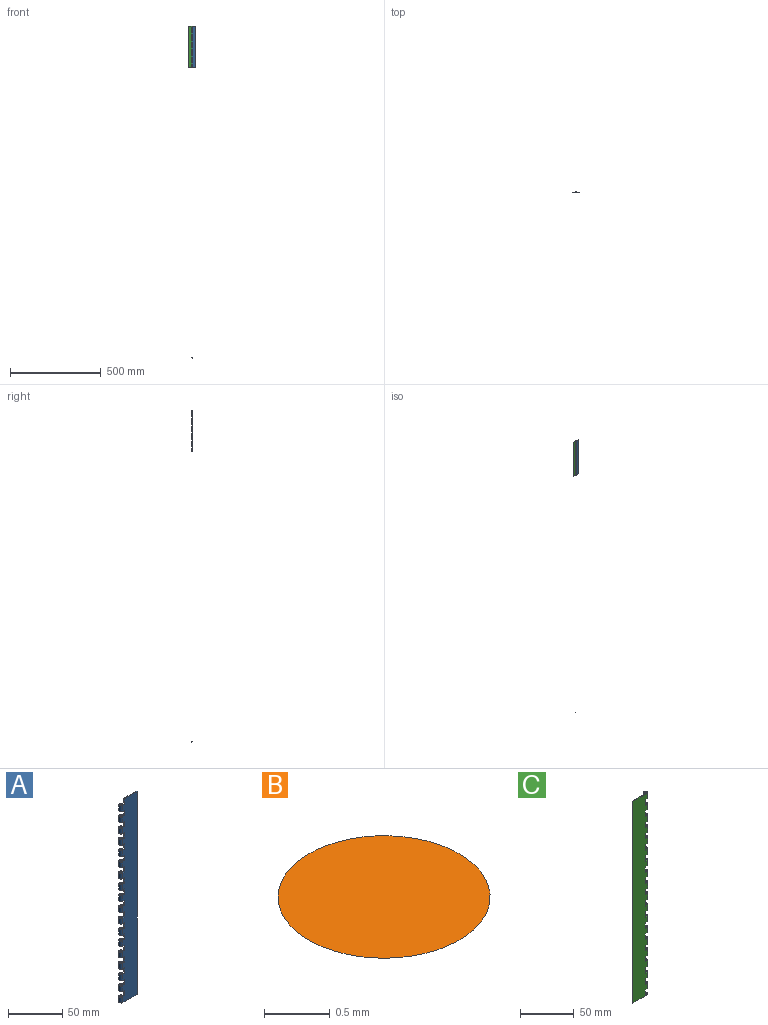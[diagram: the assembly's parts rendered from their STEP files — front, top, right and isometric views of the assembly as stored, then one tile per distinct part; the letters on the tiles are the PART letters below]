
ASSEMBLY  parts=3 mates=2
PART A: 96 faces, bbox 21x3.9x228.8 mm
  f0: plane 228.8x17.4mm, normal (0,1,0), area 3893.9mm2, adj f2,f3,f5,f7,f9,f11,f13,f15
  f1: plane 228.8x19.05mm, normal (0,-1,0), area 4081.5mm2, adj f2,f3,f5,f7,f9,f11,f13,f15
  f2: plane 228.8x0.89mm, normal (1,0,0), area 203.4mm2, adj f0,f1,f39,f95
  f3: cylinder r=1.97mm len=6.33mm, axis (0,0,-1), area 66mm2, adj f0,f1,f91,f94
  f4: cylinder r=1.08mm len=6.33mm, axis (0,0,-1), area 42.9mm2, adj f91,f94
  f5: cylinder r=1.97mm len=6.33mm, axis (0,0,-1), area 66mm2, adj f0,f1,f88,f92
  f6: cylinder r=1.08mm len=6.33mm, axis (0,0,-1), area 42.9mm2, adj f88,f92
  f7: cylinder r=1.97mm len=6.33mm, axis (0,0,-1), area 66mm2, adj f0,f1,f85,f89
  f8: cylinder r=1.08mm len=6.33mm, axis (0,0,-1), area 42.9mm2, adj f85,f89
  f9: cylinder r=1.97mm len=6.33mm, axis (0,0,-1), area 66mm2, adj f0,f1,f82,f86
  f10: cylinder r=1.08mm len=6.33mm, axis (0,0,-1), area 42.9mm2, adj f82,f86
  f11: cylinder r=1.97mm len=6.33mm, axis (0,0,-1), area 66mm2, adj f0,f1,f79,f83
  f12: cylinder r=1.08mm len=6.33mm, axis (0,0,-1), area 42.9mm2, adj f79,f83
  f13: cylinder r=1.97mm len=6.33mm, axis (0,0,-1), area 66mm2, adj f0,f1,f76,f80
  f14: cylinder r=1.08mm len=6.33mm, axis (0,0,-1), area 42.9mm2, adj f76,f80
  f15: cylinder r=1.97mm len=6.33mm, axis (0,0,-1), area 66mm2, adj f0,f1,f73,f77
  f16: cylinder r=1.08mm len=6.33mm, axis (0,0,-1), area 42.9mm2, adj f73,f77
  f17: cylinder r=1.97mm len=6.33mm, axis (0,0,-1), area 66mm2, adj f0,f1,f70,f74
  f18: cylinder r=1.08mm len=6.33mm, axis (0,0,-1), area 42.9mm2, adj f70,f74
  f19: cylinder r=1.97mm len=6.33mm, axis (0,0,-1), area 66mm2, adj f0,f1,f67,f71
  f20: cylinder r=1.08mm len=6.33mm, axis (0,0,-1), area 42.9mm2, adj f67,f71
  f21: cylinder r=1.97mm len=6.33mm, axis (0,0,-1), area 66mm2, adj f0,f1,f64,f68
  f22: cylinder r=1.08mm len=6.33mm, axis (0,0,-1), area 42.9mm2, adj f64,f68
  f23: cylinder r=1.97mm len=6.33mm, axis (0,0,-1), area 66mm2, adj f0,f1,f61,f65
  f24: cylinder r=1.08mm len=6.33mm, axis (0,0,-1), area 42.9mm2, adj f61,f65
  f25: cylinder r=1.97mm len=6.33mm, axis (0,0,-1), area 66mm2, adj f0,f1,f58,f62
  f26: cylinder r=1.08mm len=6.33mm, axis (0,0,-1), area 42.9mm2, adj f58,f62
  f27: cylinder r=1.97mm len=6.33mm, axis (0,0,-1), area 66mm2, adj f0,f1,f55,f59
  f28: cylinder r=1.08mm len=6.33mm, axis (0,0,-1), area 42.9mm2, adj f55,f59
  f29: cylinder r=1.97mm len=6.33mm, axis (0,0,-1), area 66mm2, adj f0,f1,f52,f56
  f30: cylinder r=1.08mm len=6.33mm, axis (0,0,-1), area 42.9mm2, adj f52,f56
  f31: cylinder r=1.97mm len=6.33mm, axis (0,0,-1), area 66mm2, adj f0,f1,f49,f53
  f32: cylinder r=1.08mm len=6.33mm, axis (0,0,-1), area 42.9mm2, adj f49,f53
  f33: cylinder r=1.97mm len=6.33mm, axis (0,0,-1), area 66mm2, adj f0,f1,f46,f50
  f34: cylinder r=1.08mm len=6.33mm, axis (0,0,-1), area 42.9mm2, adj f46,f50
  f35: cylinder r=1.97mm len=6.33mm, axis (0,0,-1), area 66mm2, adj f0,f1,f43,f47
  f36: cylinder r=1.08mm len=6.33mm, axis (0,0,-1), area 42.9mm2, adj f43,f47
  f37: cylinder r=1.97mm len=6.33mm, axis (0,0,-1), area 66mm2, adj f0,f1,f40,f44
  f38: cylinder r=1.08mm len=6.33mm, axis (0,0,-1), area 42.9mm2, adj f40,f44
  f39: plane 16.64x0.89mm, normal (0,0,1), area 14.8mm2, adj f0,f1,f2,f41
  f40: plane 4.38x3.94mm, normal (0,0,1), area 9.6mm2, adj f0,f1,f37,f38,f41
  f41: plane 6.37x0.89mm, normal (-1,0,0), area 5.7mm2, adj f0,f1,f39,f40
  f42: plane 6.37x0.89mm, normal (-1,0,0), area 5.7mm2, adj f0,f1,f43,f44
  f43: plane 4.38x3.94mm, normal (0,0,1), area 9.6mm2, adj f0,f1,f35,f36,f42
  f44: plane 4.38x3.94mm, normal (0,0,-1), area 9.6mm2, adj f0,f1,f37,f38,f42
  f45: plane 6.37x0.89mm, normal (-1,0,0), area 5.7mm2, adj f0,f1,f46,f47
  f46: plane 4.38x3.94mm, normal (0,0,1), area 9.6mm2, adj f0,f1,f33,f34,f45
  f47: plane 4.38x3.94mm, normal (0,0,-1), area 9.6mm2, adj f0,f1,f35,f36,f45
  f48: plane 6.37x0.89mm, normal (-1,0,0), area 5.7mm2, adj f0,f1,f49,f50
  f49: plane 4.38x3.94mm, normal (0,0,1), area 9.6mm2, adj f0,f1,f31,f32,f48
  f50: plane 4.38x3.94mm, normal (0,0,-1), area 9.6mm2, adj f0,f1,f33,f34,f48
  f51: plane 6.37x0.89mm, normal (-1,0,0), area 5.7mm2, adj f0,f1,f52,f53
  f52: plane 4.38x3.94mm, normal (0,0,1), area 9.6mm2, adj f0,f1,f29,f30,f51
  f53: plane 4.38x3.94mm, normal (0,0,-1), area 9.6mm2, adj f0,f1,f31,f32,f51
  f54: plane 6.37x0.89mm, normal (-1,0,0), area 5.7mm2, adj f0,f1,f55,f56
  f55: plane 4.38x3.94mm, normal (0,0,1), area 9.6mm2, adj f0,f1,f27,f28,f54
  f56: plane 4.38x3.94mm, normal (0,0,-1), area 9.6mm2, adj f0,f1,f29,f30,f54
  f57: plane 6.37x0.89mm, normal (-1,0,0), area 5.7mm2, adj f0,f1,f58,f59
  f58: plane 4.38x3.94mm, normal (0,0,1), area 9.6mm2, adj f0,f1,f25,f26,f57
  f59: plane 4.38x3.94mm, normal (0,0,-1), area 9.6mm2, adj f0,f1,f27,f28,f57
  f60: plane 6.37x0.89mm, normal (-1,0,0), area 5.7mm2, adj f0,f1,f61,f62
  f61: plane 4.38x3.94mm, normal (0,0,1), area 9.6mm2, adj f0,f1,f23,f24,f60
  f62: plane 4.38x3.94mm, normal (0,0,-1), area 9.6mm2, adj f0,f1,f25,f26,f60
  f63: plane 6.37x0.89mm, normal (-1,0,0), area 5.7mm2, adj f0,f1,f64,f65
  f64: plane 4.38x3.94mm, normal (0,0,1), area 9.6mm2, adj f0,f1,f21,f22,f63
  f65: plane 4.38x3.94mm, normal (0,0,-1), area 9.6mm2, adj f0,f1,f23,f24,f63
  f66: plane 6.37x0.89mm, normal (-1,0,0), area 5.7mm2, adj f0,f1,f67,f68
  f67: plane 4.38x3.94mm, normal (0,0,1), area 9.6mm2, adj f0,f1,f19,f20,f66
  f68: plane 4.38x3.94mm, normal (0,0,-1), area 9.6mm2, adj f0,f1,f21,f22,f66
  f69: plane 6.37x0.89mm, normal (-1,0,0), area 5.7mm2, adj f0,f1,f70,f71
  f70: plane 4.38x3.94mm, normal (0,0,1), area 9.6mm2, adj f0,f1,f17,f18,f69
  f71: plane 4.38x3.94mm, normal (0,0,-1), area 9.6mm2, adj f0,f1,f19,f20,f69
  f72: plane 6.37x0.89mm, normal (-1,0,0), area 5.7mm2, adj f0,f1,f73,f74
  f73: plane 4.38x3.94mm, normal (0,0,1), area 9.6mm2, adj f0,f1,f15,f16,f72
  f74: plane 4.38x3.94mm, normal (0,0,-1), area 9.6mm2, adj f0,f1,f17,f18,f72
  f75: plane 6.37x0.89mm, normal (-1,0,0), area 5.7mm2, adj f0,f1,f76,f77
  f76: plane 4.38x3.94mm, normal (0,0,1), area 9.6mm2, adj f0,f1,f13,f14,f75
  f77: plane 4.38x3.94mm, normal (0,0,-1), area 9.6mm2, adj f0,f1,f15,f16,f75
  f78: plane 6.37x0.89mm, normal (-1,0,0), area 5.7mm2, adj f0,f1,f79,f80
  f79: plane 4.38x3.94mm, normal (0,0,1), area 9.6mm2, adj f0,f1,f11,f12,f78
  f80: plane 4.38x3.94mm, normal (0,0,-1), area 9.6mm2, adj f0,f1,f13,f14,f78
  f81: plane 6.37x0.89mm, normal (-1,0,0), area 5.7mm2, adj f0,f1,f82,f83
  f82: plane 4.38x3.94mm, normal (0,0,1), area 9.6mm2, adj f0,f1,f9,f10,f81
  f83: plane 4.38x3.94mm, normal (0,0,-1), area 9.6mm2, adj f0,f1,f11,f12,f81
  f84: plane 6.37x0.89mm, normal (-1,0,0), area 5.7mm2, adj f0,f1,f85,f86
  f85: plane 4.38x3.94mm, normal (0,0,1), area 9.6mm2, adj f0,f1,f7,f8,f84
  f86: plane 4.38x3.94mm, normal (0,0,-1), area 9.6mm2, adj f0,f1,f9,f10,f84
  f87: plane 6.37x0.89mm, normal (-1,0,0), area 5.7mm2, adj f0,f1,f88,f89
  f88: plane 4.38x3.94mm, normal (0,0,1), area 9.6mm2, adj f0,f1,f5,f6,f87
  f89: plane 4.38x3.94mm, normal (0,0,-1), area 9.6mm2, adj f0,f1,f7,f8,f87
  f90: plane 6.37x0.89mm, normal (-1,0,0), area 5.7mm2, adj f0,f1,f91,f92
  f91: plane 4.38x3.94mm, normal (0,0,1), area 9.6mm2, adj f0,f1,f3,f4,f90
  f92: plane 4.38x3.94mm, normal (0,0,-1), area 9.6mm2, adj f0,f1,f5,f6,f90
  f93: plane 0.89x0.2mm, normal (-1,0,0), area 0.2mm2, adj f0,f1,f94,f95
  f94: plane 4.38x3.94mm, normal (0,0,-1), area 9.6mm2, adj f0,f1,f3,f4,f93
  f95: plane 16.64x0.89mm, normal (0,0,-1), area 14.8mm2, adj f0,f1,f2,f93
PART B: 2 faces, bbox 1.6x1.6x0.3 mm
  f0: sphere r=1.4mm, area 2.2mm2, adj f1
  f1: plane 1.61x1.61mm, normal (0,0,1), area 2mm2, adj f0
PART C: 97 faces, bbox 21x3.9x228.8 mm
  f0: plane 228.8x17.4mm, normal (0,1,0), area 3894.1mm2, adj f3,f5,f7,f9,f11,f13,f15,f17
  f1: plane 228.8x19.05mm, normal (0,-1,0), area 4082mm2, adj f3,f5,f7,f9,f11,f13,f15,f17
  f2: cylinder r=1.08mm len=2.16mm, axis (0,0,-1), area 1.2mm2, adj f94,f96
  f3: cylinder r=1.97mm len=3.94mm, axis (0,0,-1), area 1.9mm2, adj f0,f1,f94,f96
  f4: cylinder r=1.08mm len=6.33mm, axis (0,0,-1), area 42.9mm2, adj f91,f95
  f5: cylinder r=1.97mm len=6.33mm, axis (0,0,-1), area 66mm2, adj f0,f1,f91,f95
  f6: cylinder r=1.08mm len=6.33mm, axis (0,0,-1), area 42.9mm2, adj f88,f92
  f7: cylinder r=1.97mm len=6.33mm, axis (0,0,-1), area 66mm2, adj f0,f1,f88,f92
  f8: cylinder r=1.08mm len=6.33mm, axis (0,0,-1), area 42.9mm2, adj f85,f89
  f9: cylinder r=1.97mm len=6.33mm, axis (0,0,-1), area 66mm2, adj f0,f1,f85,f89
  f10: cylinder r=1.08mm len=6.33mm, axis (0,0,-1), area 42.9mm2, adj f82,f86
  f11: cylinder r=1.97mm len=6.33mm, axis (0,0,-1), area 66mm2, adj f0,f1,f82,f86
  f12: cylinder r=1.08mm len=6.33mm, axis (0,0,-1), area 42.9mm2, adj f79,f83
  f13: cylinder r=1.97mm len=6.33mm, axis (0,0,-1), area 66mm2, adj f0,f1,f79,f83
  f14: cylinder r=1.08mm len=6.33mm, axis (0,0,-1), area 42.9mm2, adj f76,f80
  f15: cylinder r=1.97mm len=6.33mm, axis (0,0,-1), area 66mm2, adj f0,f1,f76,f80
  f16: cylinder r=1.08mm len=6.33mm, axis (0,0,-1), area 42.9mm2, adj f73,f77
  f17: cylinder r=1.97mm len=6.33mm, axis (0,0,-1), area 66mm2, adj f0,f1,f73,f77
  f18: cylinder r=1.08mm len=6.33mm, axis (0,0,-1), area 42.9mm2, adj f70,f74
  f19: cylinder r=1.97mm len=6.33mm, axis (0,0,-1), area 66mm2, adj f0,f1,f70,f74
  f20: cylinder r=1.08mm len=6.33mm, axis (0,0,-1), area 42.9mm2, adj f67,f71
  f21: cylinder r=1.97mm len=6.33mm, axis (0,0,-1), area 66mm2, adj f0,f1,f67,f71
  f22: cylinder r=1.08mm len=6.33mm, axis (0,0,-1), area 42.9mm2, adj f64,f68
  f23: cylinder r=1.97mm len=6.33mm, axis (0,0,-1), area 66mm2, adj f0,f1,f64,f68
  f24: cylinder r=1.08mm len=6.33mm, axis (0,0,-1), area 42.9mm2, adj f61,f65
  f25: cylinder r=1.97mm len=6.33mm, axis (0,0,-1), area 66mm2, adj f0,f1,f61,f65
  f26: cylinder r=1.08mm len=6.33mm, axis (0,0,-1), area 42.9mm2, adj f58,f62
  f27: cylinder r=1.97mm len=6.33mm, axis (0,0,-1), area 66mm2, adj f0,f1,f58,f62
  f28: cylinder r=1.08mm len=6.33mm, axis (0,0,-1), area 42.9mm2, adj f55,f59
  f29: cylinder r=1.97mm len=6.33mm, axis (0,0,-1), area 66mm2, adj f0,f1,f55,f59
  f30: cylinder r=1.08mm len=6.33mm, axis (0,0,-1), area 42.9mm2, adj f52,f56
  f31: cylinder r=1.97mm len=6.33mm, axis (0,0,-1), area 66mm2, adj f0,f1,f52,f56
  f32: cylinder r=1.08mm len=6.33mm, axis (0,0,-1), area 42.9mm2, adj f49,f53
  f33: cylinder r=1.97mm len=6.33mm, axis (0,0,-1), area 66mm2, adj f0,f1,f49,f53
  f34: cylinder r=1.08mm len=6.33mm, axis (0,0,-1), area 42.9mm2, adj f46,f50
  f35: cylinder r=1.97mm len=6.33mm, axis (0,0,-1), area 66mm2, adj f0,f1,f46,f50
  f36: cylinder r=1.08mm len=6.33mm, axis (0,0,-1), area 42.9mm2, adj f43,f47
  f37: cylinder r=1.97mm len=6.33mm, axis (0,0,-1), area 66mm2, adj f0,f1,f43,f47
  f38: cylinder r=1.08mm len=6.35mm, axis (0,0,-1), area 43.1mm2, adj f41,f44
  f39: cylinder r=1.97mm len=6.35mm, axis (0,0,-1), area 66.2mm2, adj f0,f1,f41,f44
  f40: plane 228.8x0.89mm, normal (-1,0,0), area 203.4mm2, adj f0,f1,f41,f96
  f41: plane 21.02x3.94mm, normal (0,0,1), area 24.4mm2, adj f0,f1,f38,f39,f40
  f42: plane 6.37x0.89mm, normal (1,0,0), area 5.7mm2, adj f0,f1,f43,f44
  f43: plane 4.38x3.94mm, normal (0,0,1), area 9.6mm2, adj f0,f1,f36,f37,f42
  f44: plane 4.38x3.94mm, normal (0,0,-1), area 9.6mm2, adj f0,f1,f38,f39,f42
  f45: plane 6.37x0.89mm, normal (1,0,0), area 5.7mm2, adj f0,f1,f46,f47
  f46: plane 4.38x3.94mm, normal (0,0,1), area 9.6mm2, adj f0,f1,f34,f35,f45
  f47: plane 4.38x3.94mm, normal (0,0,-1), area 9.6mm2, adj f0,f1,f36,f37,f45
  f48: plane 6.37x0.89mm, normal (1,0,0), area 5.7mm2, adj f0,f1,f49,f50
  f49: plane 4.38x3.94mm, normal (0,0,1), area 9.6mm2, adj f0,f1,f32,f33,f48
  f50: plane 4.38x3.94mm, normal (0,0,-1), area 9.6mm2, adj f0,f1,f34,f35,f48
  f51: plane 6.37x0.89mm, normal (1,0,0), area 5.7mm2, adj f0,f1,f52,f53
  f52: plane 4.38x3.94mm, normal (0,0,1), area 9.6mm2, adj f0,f1,f30,f31,f51
  f53: plane 4.38x3.94mm, normal (0,0,-1), area 9.6mm2, adj f0,f1,f32,f33,f51
  f54: plane 6.37x0.89mm, normal (1,0,0), area 5.7mm2, adj f0,f1,f55,f56
  f55: plane 4.38x3.94mm, normal (0,0,1), area 9.6mm2, adj f0,f1,f28,f29,f54
  f56: plane 4.38x3.94mm, normal (0,0,-1), area 9.6mm2, adj f0,f1,f30,f31,f54
  f57: plane 6.37x0.89mm, normal (1,0,0), area 5.7mm2, adj f0,f1,f58,f59
  f58: plane 4.38x3.94mm, normal (0,0,1), area 9.6mm2, adj f0,f1,f26,f27,f57
  f59: plane 4.38x3.94mm, normal (0,0,-1), area 9.6mm2, adj f0,f1,f28,f29,f57
  f60: plane 6.37x0.89mm, normal (1,0,0), area 5.7mm2, adj f0,f1,f61,f62
  f61: plane 4.38x3.94mm, normal (0,0,1), area 9.6mm2, adj f0,f1,f24,f25,f60
  f62: plane 4.38x3.94mm, normal (0,0,-1), area 9.6mm2, adj f0,f1,f26,f27,f60
  f63: plane 6.37x0.89mm, normal (1,0,0), area 5.7mm2, adj f0,f1,f64,f65
  f64: plane 4.38x3.94mm, normal (0,0,1), area 9.6mm2, adj f0,f1,f22,f23,f63
  f65: plane 4.38x3.94mm, normal (0,0,-1), area 9.6mm2, adj f0,f1,f24,f25,f63
  f66: plane 6.37x0.89mm, normal (1,0,0), area 5.7mm2, adj f0,f1,f67,f68
  f67: plane 4.38x3.94mm, normal (0,0,1), area 9.6mm2, adj f0,f1,f20,f21,f66
  f68: plane 4.38x3.94mm, normal (0,0,-1), area 9.6mm2, adj f0,f1,f22,f23,f66
  f69: plane 6.37x0.89mm, normal (1,0,0), area 5.7mm2, adj f0,f1,f70,f71
  f70: plane 4.38x3.94mm, normal (0,0,1), area 9.6mm2, adj f0,f1,f18,f19,f69
  f71: plane 4.38x3.94mm, normal (0,0,-1), area 9.6mm2, adj f0,f1,f20,f21,f69
  f72: plane 6.37x0.89mm, normal (1,0,0), area 5.7mm2, adj f0,f1,f73,f74
  f73: plane 4.38x3.94mm, normal (0,0,1), area 9.6mm2, adj f0,f1,f16,f17,f72
  f74: plane 4.38x3.94mm, normal (0,0,-1), area 9.6mm2, adj f0,f1,f18,f19,f72
  f75: plane 6.37x0.89mm, normal (1,0,0), area 5.7mm2, adj f0,f1,f76,f77
  f76: plane 4.38x3.94mm, normal (0,0,1), area 9.6mm2, adj f0,f1,f14,f15,f75
  f77: plane 4.38x3.94mm, normal (0,0,-1), area 9.6mm2, adj f0,f1,f16,f17,f75
  f78: plane 6.37x0.89mm, normal (1,0,0), area 5.7mm2, adj f0,f1,f79,f80
  f79: plane 4.38x3.94mm, normal (0,0,1), area 9.6mm2, adj f0,f1,f12,f13,f78
  f80: plane 4.38x3.94mm, normal (0,0,-1), area 9.6mm2, adj f0,f1,f14,f15,f78
  f81: plane 6.37x0.89mm, normal (1,0,0), area 5.7mm2, adj f0,f1,f82,f83
  f82: plane 4.38x3.94mm, normal (0,0,1), area 9.6mm2, adj f0,f1,f10,f11,f81
  f83: plane 4.38x3.94mm, normal (0,0,-1), area 9.6mm2, adj f0,f1,f12,f13,f81
  f84: plane 6.37x0.89mm, normal (1,0,0), area 5.7mm2, adj f0,f1,f85,f86
  f85: plane 4.38x3.94mm, normal (0,0,1), area 9.6mm2, adj f0,f1,f8,f9,f84
  f86: plane 4.38x3.94mm, normal (0,0,-1), area 9.6mm2, adj f0,f1,f10,f11,f84
  f87: plane 6.37x0.89mm, normal (1,0,0), area 5.7mm2, adj f0,f1,f88,f89
  f88: plane 4.38x3.94mm, normal (0,0,1), area 9.6mm2, adj f0,f1,f6,f7,f87
  f89: plane 4.38x3.94mm, normal (0,0,-1), area 9.6mm2, adj f0,f1,f8,f9,f87
  f90: plane 6.37x0.89mm, normal (1,0,0), area 5.7mm2, adj f0,f1,f91,f92
  f91: plane 4.38x3.94mm, normal (0,0,1), area 9.6mm2, adj f0,f1,f4,f5,f90
  f92: plane 4.38x3.94mm, normal (0,0,-1), area 9.6mm2, adj f0,f1,f6,f7,f90
  f93: plane 6.37x0.89mm, normal (1,0,0), area 5.7mm2, adj f0,f1,f94,f95
  f94: plane 4.38x3.94mm, normal (0,0,1), area 9.6mm2, adj f0,f1,f2,f3,f93
  f95: plane 4.38x3.94mm, normal (0,0,-1), area 9.6mm2, adj f0,f1,f4,f5,f93
  f96: plane 21.02x3.94mm, normal (0,0,-1), area 24.4mm2, adj f0,f1,f2,f3,f40
PLACE A t=(-490.6,-7.84,-505.69)mm
PLACE B t=(-490.6,-5.88,-505.71)mm
PLACE C t=(-490.6,-7.84,-505.71)mm fixed
MATE revolute B.f0 <-> C.f2  axis (0,0,-1) through (-490.6,-5.88,1323.09)mm
MATE revolute A.f4 <-> C.f2  axis (0,0,1) through (-490.6,-5.88,1316.74)mm
